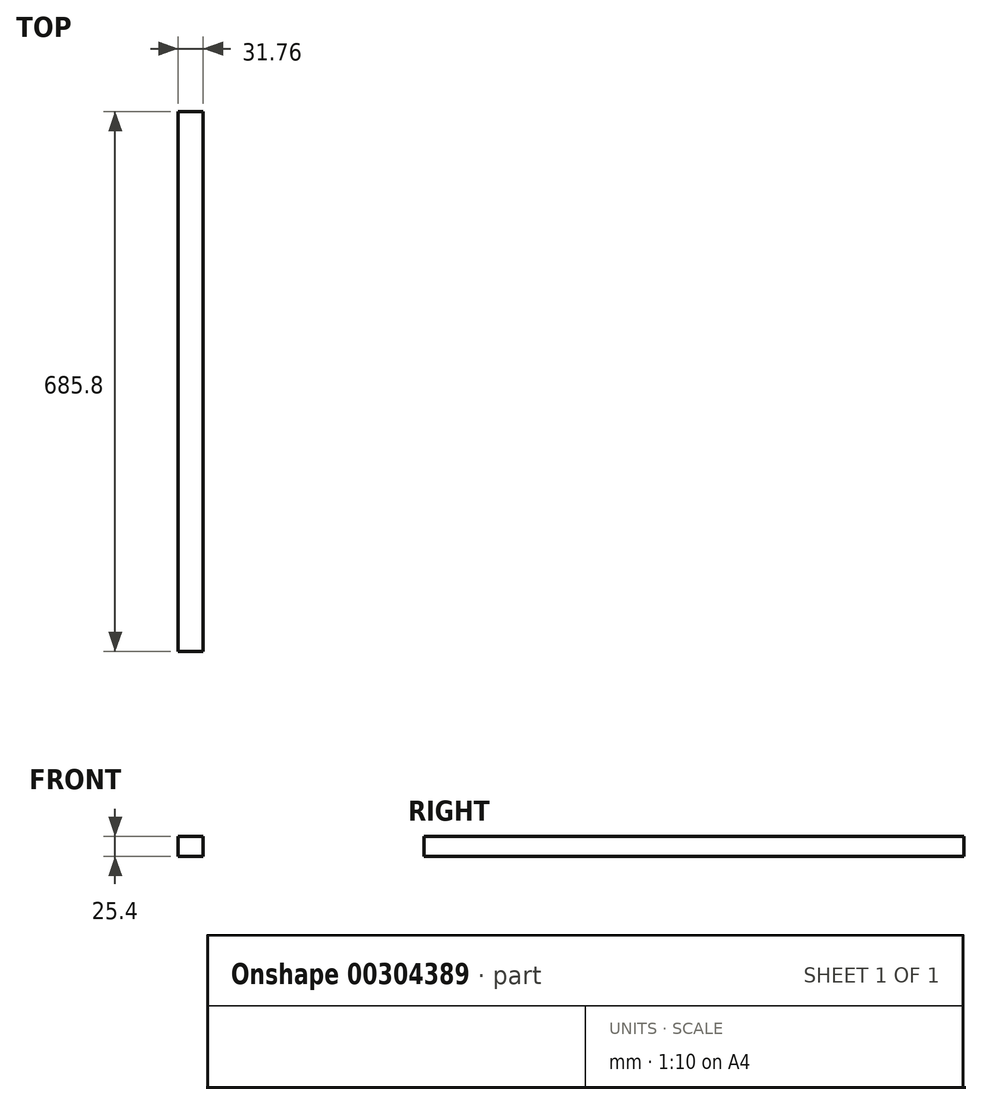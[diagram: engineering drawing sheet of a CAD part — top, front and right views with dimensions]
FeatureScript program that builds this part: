
annotation { "Feature Type Name" : "Feature", "Feature Type Description" : "" }
export const myFeature = defineFeature(function(context is Context, id is Id, definition is map)
    precondition{}
    {
        {
            var Q0;
            Q0=qCreatedBy(makeId("Top.planeOp"),FACE);
            var sketch = newSketch(context, id + "F0", { "sketchPlane" : qUnion([Q0])});
            skLineSegment(sketch, "E0.bottom", {"start": v(-15.88, 342.9) * mm, "end": v(15.87, 342.9) * mm});
            skLineSegment(sketch, "E0.top", {"start": v(-15.88, -342.9) * mm, "end": v(15.87, -342.9) * mm});
            skLineSegment(sketch, "E0.left", {"start": v(-15.88, 342.9) * mm, "end": v(-15.88, -342.9) * mm});
            skLineSegment(sketch, "E0.right", {"start": v(15.87, 342.9) * mm, "end": v(15.87, -342.9) * mm});
            skPoint(sketch, "E0.middle", {"position": v(0, 0) * mm});
            skSolve(sketch);
        }
        {
            var Q0;
            Q0=makeQuery(id+"F0.imprint","IMPRINT",FACE,{"disambiguationData":[TD([[makeQuery(id+"F0.imprint","IMPRINT",EDGE,{"derivedFrom":sQuery(id+"F0.wireOp",EDGE,"E0.bottom")}),-1.0]])]});
            extrude(context, id + "F1", {"entities" : qUnion([Q0]), "depth" : 25.4 * mm});
        }
    });
